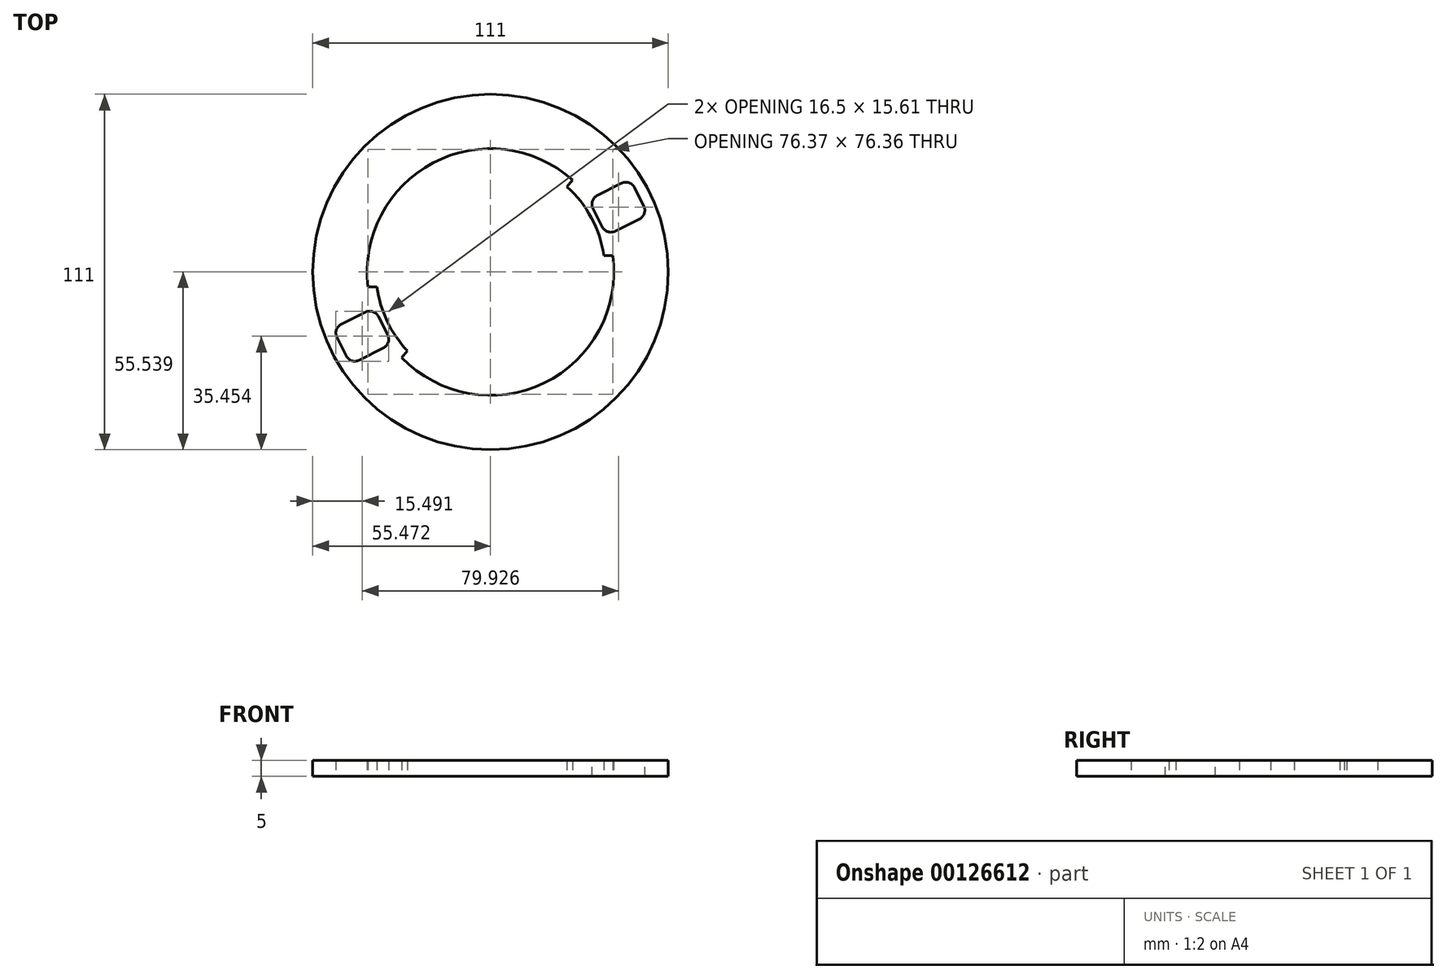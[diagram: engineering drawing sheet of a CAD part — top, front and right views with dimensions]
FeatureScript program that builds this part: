
annotation { "Feature Type Name" : "Feature", "Feature Type Description" : "" }
export const myFeature = defineFeature(function(context is Context, id is Id, definition is map)
    precondition{}
    {
        {
            var Q0;
            Q0=qCreatedBy(makeId("Top.planeOp"),FACE);
            var sketch = newSketch(context, id + "F0", { "sketchPlane" : qUnion([Q0])});
            skCircle(sketch, "E0", {"center": v(0, 0) * mm, "radius": 55.5 * mm});
            skLineSegment(sketch, "E1", {"start": v(0, 0) * mm, "end": v(49.52, 25.07) * mm, "construction": true});
            skLineSegment(sketch, "E2", {"start": v(49.52, 25.07) * mm, "end": v(-49.6, -24.88) * mm, "construction": true});
            skLineSegment(sketch, "E3", {"start": v(-46.48, -23.3) * mm, "end": v(-43.67, -28.89) * mm});
            skLineSegment(sketch, "E4", {"start": v(-46.48, -23.3) * mm, "end": v(-49.3, -17.73) * mm});
            skLineSegment(sketch, "E5", {"start": v(-49.3, -17.73) * mm, "end": v(-36.35, -11.2) * mm});
            skLineSegment(sketch, "E6", {"start": v(-43.67, -28.89) * mm, "end": v(-30.72, -22.36) * mm});
            skLineSegment(sketch, "E7", {"start": v(-36.35, -11.2) * mm, "end": v(-30.72, -22.36) * mm});
            skArc(sketch, "E8", {"start": v(-35.44, -4.68) * mm, "mid": v(-32.27, -15.38) * mm, "end": v(-25.96, -24.58) * mm});
            skArc(sketch, "E9", {"start": v(-27.72, -26.72) * mm, "mid": v(16.76, -34.66) * mm, "end": v(38.16, 5.12) * mm});
            skLineSegment(sketch, "E10", {"start": v(46.39, 23.5) * mm, "end": v(46.4, 23.49) * mm});
            skLineSegment(sketch, "E11.trimOffspring", {"start": v(47.61, 21.07) * mm, "end": v(49.2, 17.91) * mm});
            skLineSegment(sketch, "E12", {"start": v(46.4, 23.49) * mm, "end": v(43.58, 29.07) * mm});
            skLineSegment(sketch, "E13", {"start": v(43.58, 29.07) * mm, "end": v(46.4, 23.49) * mm});
            skLineSegment(sketch, "E14", {"start": v(46.4, 23.49) * mm, "end": v(49.2, 17.91) * mm});
            skLineSegment(sketch, "E15", {"start": v(49.2, 17.91) * mm, "end": v(36.25, 11.39) * mm});
            skLineSegment(sketch, "E16", {"start": v(43.58, 29.07) * mm, "end": v(30.63, 22.54) * mm});
            skLineSegment(sketch, "E17", {"start": v(30.63, 22.54) * mm, "end": v(36.25, 11.39) * mm});
            skLineSegment(sketch, "E18", {"start": v(-38.21, -4.68) * mm, "end": v(-35.44, -4.68) * mm});
            skLineSegment(sketch, "E19", {"start": v(-27.72, -26.72) * mm, "end": v(-25.96, -24.58) * mm});
            skLineSegment(sketch, "E20", {"start": v(38.16, 5.12) * mm, "end": v(35.38, 5.12) * mm});
            skLineSegment(sketch, "E21", {"start": v(25.55, 28.8) * mm, "end": v(23.83, 26.65) * mm});
            skArc(sketch, "E22.trimOffspring", {"start": v(35.38, 5.12) * mm, "mid": v(31.5, 16.9) * mm, "end": v(23.83, 26.65) * mm});
            skArc(sketch, "E23.trimOffspring", {"start": v(25.55, 28.8) * mm, "mid": v(-17.9, 34.09) * mm, "end": v(-38.21, -4.68) * mm});
            skArc(sketch, "E24.trimOffspring", {"start": v(34.35, 17.4) * mm, "mid": v(34.34, 17.4) * mm, "end": v(34.33, 17.42) * mm});
            skSolve(sketch);
        }
        {
            var Q0;
            Q0=qSketchRegion(id+"F0",true);
            extrude(context, id + "F1", {"entities" : qUnion([Q0]), "depth" : 5 * mm});
        }
        {
            var Q0;
            Q0=makeQuery(id+"F1.opExtrude","SWEPT_EDGE",EDGE,{"disambiguationData":[OSD([sQuery(id+"F0.wireOp",EDGE,"E5"),sQuery(id+"F0.wireOp",EDGE,"E7")])]});
            var Q1;
            Q1=makeQuery(id+"F1.opExtrude","SWEPT_EDGE",EDGE,{"disambiguationData":[OSD([sQuery(id+"F0.wireOp",EDGE,"E4"),sQuery(id+"F0.wireOp",EDGE,"E5")])]});
            var Q2;
            Q2=makeQuery(id+"F1.opExtrude","SWEPT_EDGE",EDGE,{"disambiguationData":[OSD([sQuery(id+"F0.wireOp",EDGE,"E6"),sQuery(id+"F0.wireOp",EDGE,"E7")])]});
            var Q3;
            Q3=makeQuery(id+"F1.opExtrude","SWEPT_EDGE",EDGE,{"disambiguationData":[OSD([sQuery(id+"F0.wireOp",EDGE,"E3"),sQuery(id+"F0.wireOp",EDGE,"E6")])]});
            var Q4;
            Q4=makeQuery(id+"F1.opExtrude","SWEPT_EDGE",EDGE,{"disambiguationData":[OSD([sQuery(id+"F0.wireOp",EDGE,"E15"),sQuery(id+"F0.wireOp",EDGE,"E17")])]});
            var Q5;
            Q5=makeQuery(id+"F1.opExtrude","SWEPT_EDGE",EDGE,{"disambiguationData":[OSD([sQuery(id+"F0.wireOp",EDGE,"E16"),sQuery(id+"F0.wireOp",EDGE,"E17")])]});
            var Q6;
            Q6=makeQuery(id+"F1.opExtrude","SWEPT_EDGE",EDGE,{"disambiguationData":[OSD([sQuery(id+"F0.wireOp",EDGE,"E13"),sQuery(id+"F0.wireOp",EDGE,"E16")])]});
            var Q7;
            Q7=makeQuery(id+"F1.opExtrude","SWEPT_EDGE",EDGE,{"disambiguationData":[OSD([sQuery(id+"F0.wireOp",EDGE,"E14"),sQuery(id+"F0.wireOp",EDGE,"E15")])]});
            fillet(context, id + "F2", {"entities" : qUnion([Q0, Q1, Q2, Q3, Q4, Q5, Q6, Q7]), "radius" : 3 * mm, "tangentPropagation" : true, "allowEdgeOverflow" : false});
        }
    });
